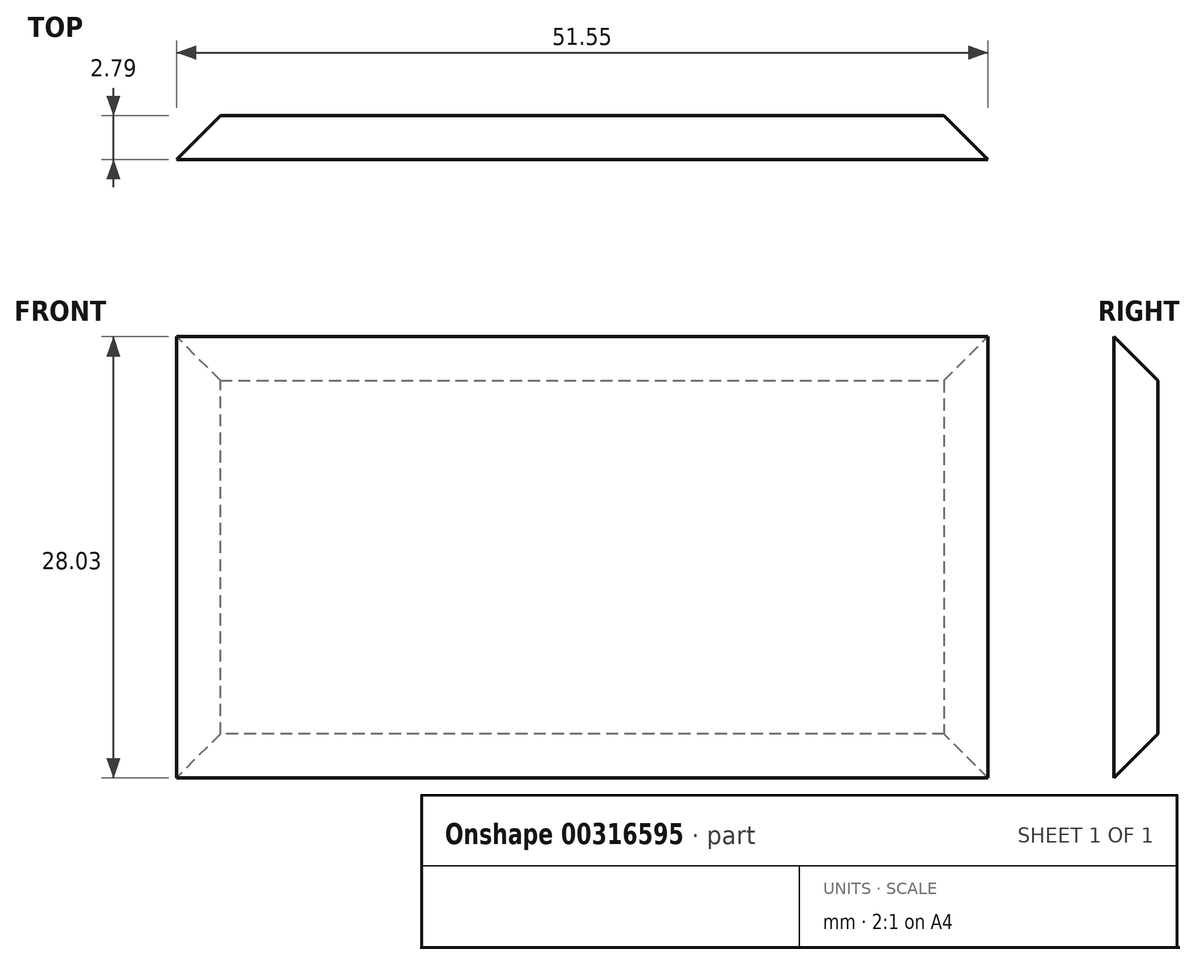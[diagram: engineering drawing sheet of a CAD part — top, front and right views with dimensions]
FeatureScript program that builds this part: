
annotation { "Feature Type Name" : "Feature", "Feature Type Description" : "" }
export const myFeature = defineFeature(function(context is Context, id is Id, definition is map)
    precondition{}
    {
        {
            var Q0;
            Q0=qCreatedBy(makeId("Front.planeOp"),FACE);
            var sketch = newSketch(context, id + "F0", { "sketchPlane" : qUnion([Q0])});
            skLineSegment(sketch, "E0.bottom", {"start": v(-3.22, 0) * mm, "end": v(-59.34, 0) * mm});
            skLineSegment(sketch, "E0.top", {"start": v(-3.22, 32.61) * mm, "end": v(-59.34, 32.61) * mm});
            skLineSegment(sketch, "E0.left", {"start": v(-3.22, 0) * mm, "end": v(-3.22, 32.61) * mm});
            skLineSegment(sketch, "E0.right", {"start": v(-59.34, 0) * mm, "end": v(-59.34, 32.61) * mm});
            skSolve(sketch);
        }
        {
            var Q0;
            Q0=makeQuery(id+"F0.imprint","IMPRINT",FACE,{"disambiguationData":[TD([[makeQuery(id+"F0.imprint","IMPRINT",EDGE,{"derivedFrom":sQuery(id+"F0.wireOp",EDGE,"E0.bottom")}),-1.0]])]});
            extrude(context, id + "F1", {"entities" : qUnion([Q0]), "depth" : 2.8 * mm});
        }
        {
            var Q0;
            Q0=makeQuery(id+"F1.opExtrude","CAP_EDGE",EDGE,{"disambiguationData":[OSD([sQuery(id+"F0.wireOp",EDGE,"E0.top")])],"isStart":true});
            var Q1;
            Q1=makeQuery(id+"F1.opExtrude","CAP_EDGE",EDGE,{"disambiguationData":[OSD([sQuery(id+"F0.wireOp",EDGE,"E0.left")])],"isStart":true});
            var Q2;
            Q2=makeQuery(id+"F1.opExtrude","CAP_FACE",FACE,{"disambiguationData":[OSD([sQuery(id+"F0.wireOp",EDGE,"E0.bottom"),sQuery(id+"F0.wireOp",EDGE,"E0.top"),sQuery(id+"F0.wireOp",EDGE,"E0.left"),sQuery(id+"F0.wireOp",EDGE,"E0.right")])],"isStart":true});
            chamfer(context, id + "F2", {"entities" : qUnion([Q0, Q1, Q2]), "width" : 5.08 * mm, "tangentPropagation" : true});
        }
    });
